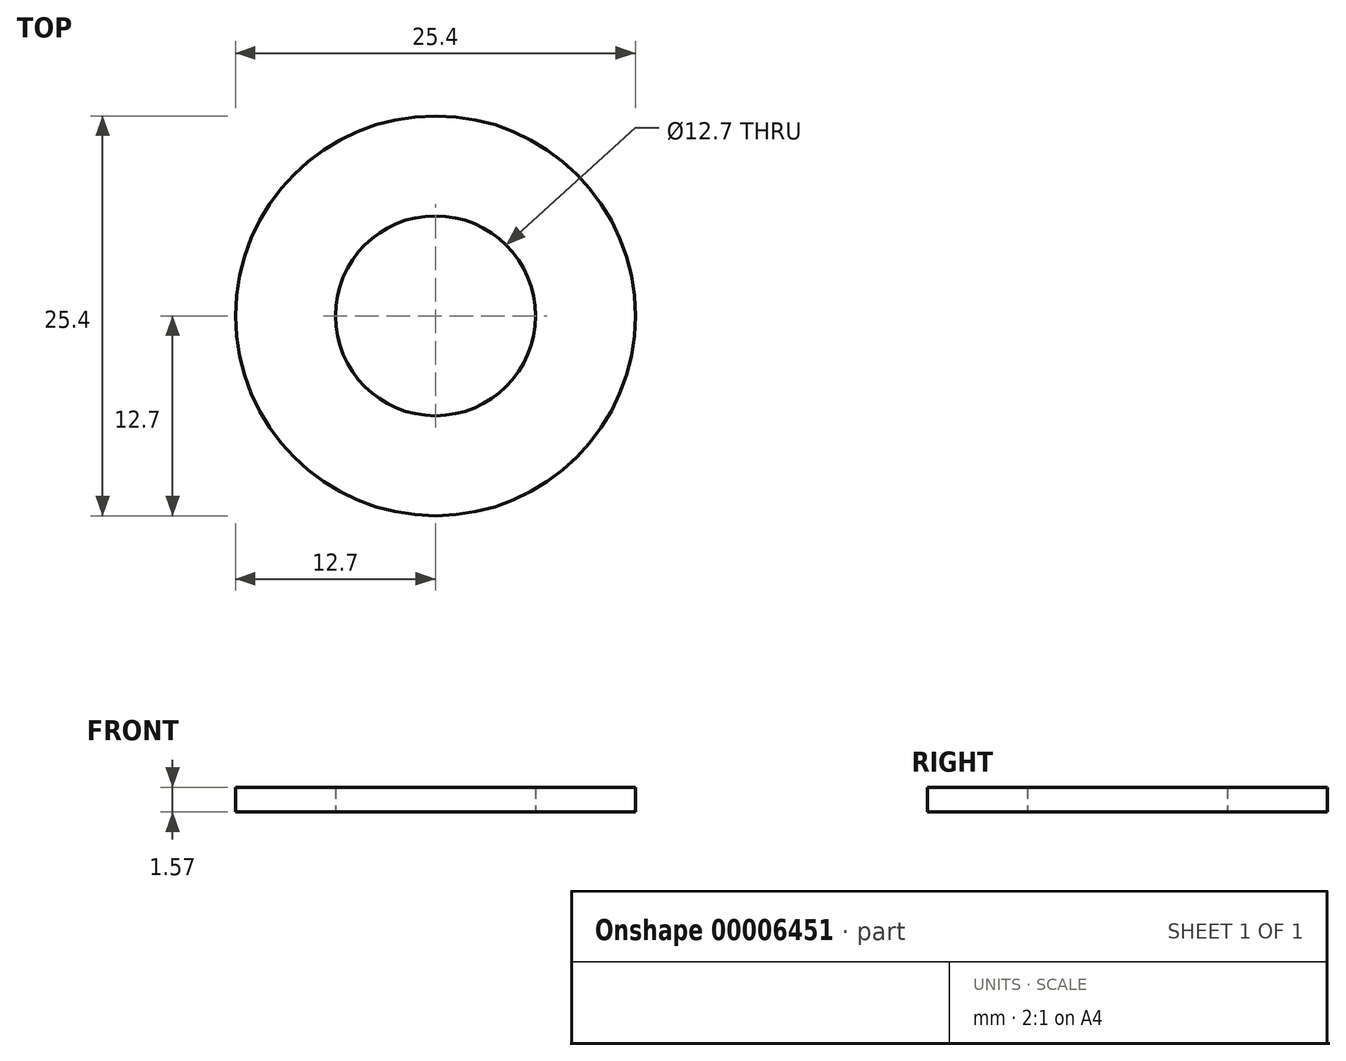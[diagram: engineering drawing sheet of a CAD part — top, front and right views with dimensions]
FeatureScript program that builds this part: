
annotation { "Feature Type Name" : "Feature", "Feature Type Description" : "" }
export const myFeature = defineFeature(function(context is Context, id is Id, definition is map)
    precondition{}
    {
        {
            var Q0;
            Q0=qCreatedBy(makeId("Top.planeOp"),FACE);
            var sketch = newSketch(context, id + "F0", { "sketchPlane" : qUnion([Q0])});
            skCircle(sketch, "E0", {"center": v(0, 0) * mm, "radius": 6.35 * mm});
            skCircle(sketch, "E1", {"center": v(0, 0) * mm, "radius": 12.7 * mm});
            skSolve(sketch);
        }
        {
            var Q0;
            Q0 = qSketchRegion(id + "F0", true);
            extrude(context, id + "F1", {"entities" : qUnion([Q0]), "depth" : 1.57 * mm});
        }
    });
